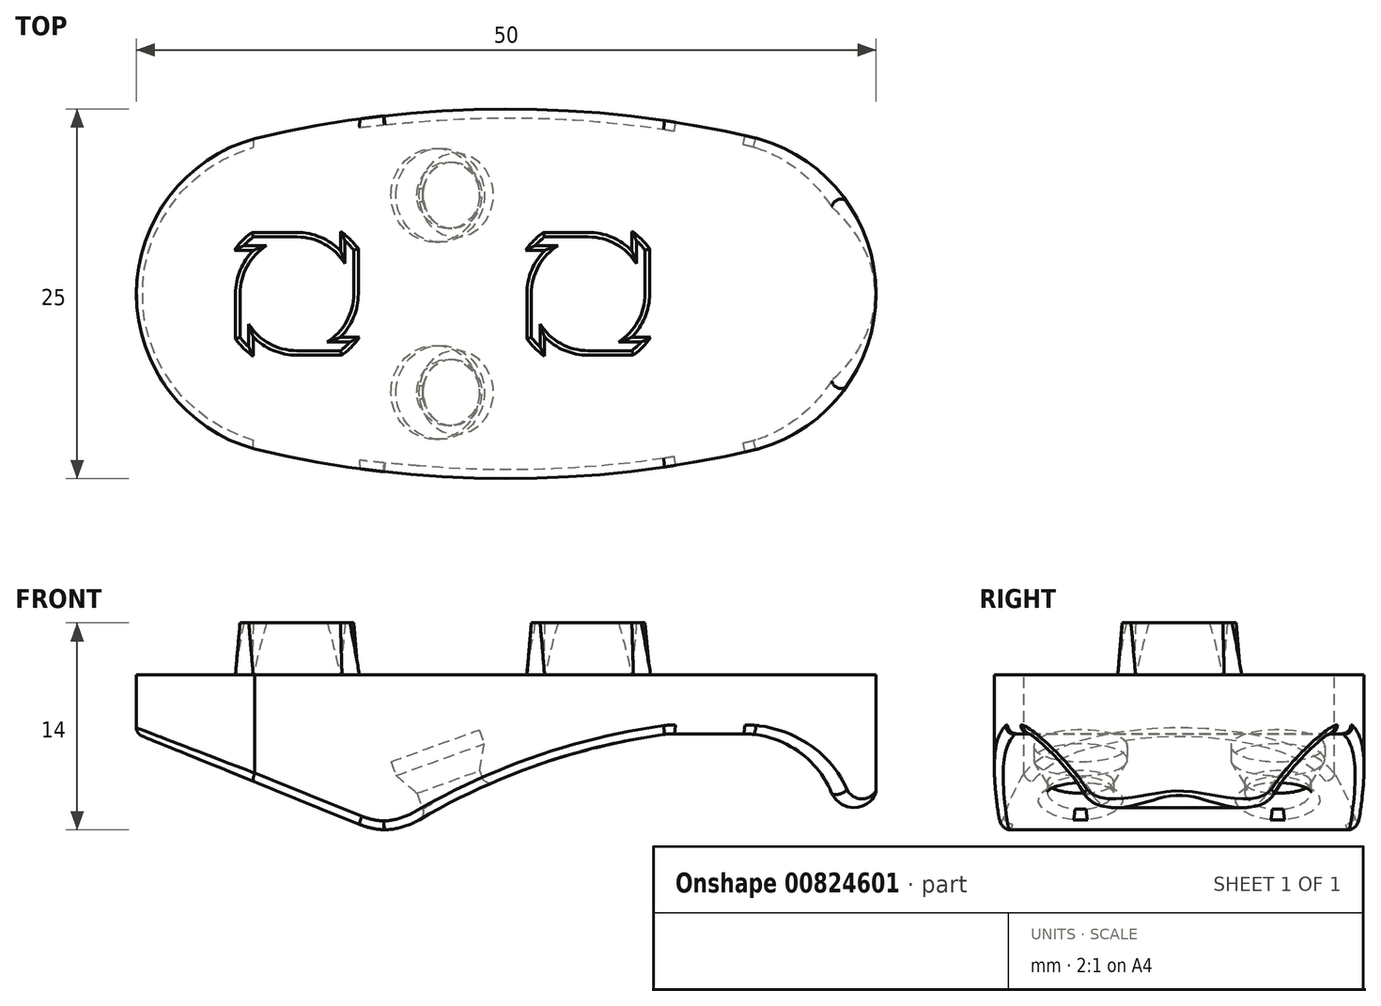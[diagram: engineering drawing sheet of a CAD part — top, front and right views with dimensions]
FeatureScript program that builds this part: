
annotation { "Feature Type Name" : "Feature", "Feature Type Description" : "" }
export const myFeature = defineFeature(function(context is Context, id is Id, definition is map)
    precondition{}
    {
        {
            var Q0;
            Q0=qCreatedBy(makeId("Front.planeOp"),FACE);
            var sketch = newSketch(context, id + "F0", { "sketchPlane" : qUnion([Q0])});
            skLineSegment(sketch, "E0", {"start": v(-12.96, 5.46) * mm, "end": v(25.04, 5.46) * mm});
            skLineSegment(sketch, "E1", {"start": v(-12.96, -7.8) * mm, "end": v(-11.16, -3.1) * mm, "construction": true});
            skLineSegment(sketch, "E2", {"start": v(-12.96, -7.8) * mm, "end": v(-12.96, 5.46) * mm});
            skLineSegment(sketch, "E3", {"start": v(0, 0) * mm, "end": v(4.11, 0) * mm});
            skArc(sketch, "E4", {"start": v(0, 0) * mm, "mid": v(-5.8, -0.8) * mm, "end": v(-11.16, -3.1) * mm});
            skArc(sketch, "E5", {"start": v(20.4, -4.8) * mm, "mid": v(12.6, -1.23) * mm, "end": v(4.11, 0) * mm});
            skLineSegment(sketch, "E6", {"start": v(20.4, -4.8) * mm, "end": v(25.04, -7.8) * mm, "construction": true});
            skLineSegment(sketch, "E7", {"start": v(25.04, -7.8) * mm, "end": v(25.04, 5.46) * mm});
            skLineSegment(sketch, "E8", {"start": v(-12.96, 3.26) * mm, "end": v(25.04, 5.46) * mm});
            skArc(sketch, "E9", {"start": v(-12.96, -3.1) * mm, "mid": v(-12.06, -3.73) * mm, "end": v(-11.16, -3.1) * mm});
            skLineSegment(sketch, "E10", {"start": v(18.4, -3.62) * mm, "end": v(25.04, -7) * mm});
            skLineSegment(sketch, "E11", {"start": v(25.04, -7) * mm, "end": v(30.04, -9.56) * mm});
            skLineSegment(sketch, "E12", {"start": v(30.04, -9.56) * mm, "end": v(30.04, 5.75) * mm});
            skLineSegment(sketch, "E13", {"start": v(25.04, 5.46) * mm, "end": v(30.04, 5.75) * mm});
            skSolve(sketch);
        }
        {
            var Q0;
            Q0=qCreatedBy(makeId("Front.planeOp"),FACE);
            var sketch = newSketch(context, id + "F1", { "sketchPlane" : qUnion([Q0])});
            skLineSegment(sketch, "E14.bottom", {"start": v(-18, 0) * mm, "end": v(18, 0) * mm});
            skLineSegment(sketch, "E14.top", {"start": v(-18, -8.5) * mm, "end": v(18, -8.5) * mm});
            skLineSegment(sketch, "E14.left", {"start": v(-18, 0) * mm, "end": v(-18, -8.5) * mm});
            skLineSegment(sketch, "E14.right", {"start": v(18, 0) * mm, "end": v(18, -8.5) * mm, "construction": true});
            skArc(sketch, "E15", {"start": v(18, -2) * mm, "mid": v(8.65, -4.28) * mm, "end": v(0, -8.5) * mm});
            skLineSegment(sketch, "E16", {"start": v(-2, -8.5) * mm, "end": v(-18, -2) * mm});
            skLineSegment(sketch, "E17", {"start": v(18, 0) * mm, "end": v(23, 0) * mm});
            skLineSegment(sketch, "E18", {"start": v(23, 0) * mm, "end": v(23, -2) * mm, "construction": true});
            skLineSegment(sketch, "E19", {"start": v(23, -2) * mm, "end": v(18, -2) * mm});
            skArc(sketch, "E20", {"start": v(29, -6) * mm, "mid": v(26.6, -3.1) * mm, "end": v(23, -2) * mm});
            skArc(sketch, "E21", {"start": v(29, -6) * mm, "mid": v(30.5, -7) * mm, "end": v(32, -6) * mm});
            skLineSegment(sketch, "E22", {"start": v(32, -6) * mm, "end": v(32, 0) * mm, "construction": true});
            skLineSegment(sketch, "E23", {"start": v(32, 0) * mm, "end": v(23, 0) * mm});
            skArc(sketch, "E24", {"start": v(32, -6) * mm, "mid": v(32.6, -3) * mm, "end": v(32, 0) * mm});
            skSolve(sketch);
        }
        {
            var Q0;
            {var subQ1=sQuery(id+"F1.wireOp",EDGE,"E14.bottom");Q0=makeQuery(id+"F1.imprint","IMPRINT",FACE,{"disambiguationData":[TD([[makeQuery(id+"F1.imprint","IMPRINT",EDGE,{"derivedFrom":subQ1}),-1.0]])]});}
            extrude(context, id + "F2", {"entities" : qUnion([Q0]), "depth" : 25 * mm, "offsetDistance" : 25 * mm});
        }
        {
            var Q0;
            Q0=makeQuery(id+"F2.opExtrude","SWEPT_FACE",FACE,{"disambiguationData":[OSD([sQuery(id+"F1.wireOp",EDGE,"E14.bottom"),sQuery(id+"F1.wireOp",EDGE,"E17"),sQuery(id+"F1.wireOp",EDGE,"E23")])]});
            var sketch = newSketch(context, id + "F3", { "sketchPlane" : qUnion([Q0])});
            skArc(sketch, "E25", {"start": v(-10, -2) * mm, "mid": v(-18, -12.5) * mm, "end": v(-10, -23) * mm});
            skArc(sketch, "E26", {"start": v(-10, -23) * mm, "mid": v(7, -25) * mm, "end": v(24, -23) * mm});
            skArc(sketch, "E27", {"start": v(24, -2) * mm, "mid": v(7, 0) * mm, "end": v(-10, -2) * mm});
            skArc(sketch, "E28", {"start": v(24, -23) * mm, "mid": v(32, -12.5) * mm, "end": v(24, -2) * mm});
            skLineSegment(sketch, "E29", {"start": v(-10, -23) * mm, "end": v(-10, -2) * mm, "construction": true});
            skLineSegment(sketch, "E30", {"start": v(-10, -23) * mm, "end": v(-10, -25) * mm, "construction": true});
            skLineSegment(sketch, "E31", {"start": v(-10, -2) * mm, "end": v(-10, 0) * mm, "construction": true});
            skLineSegment(sketch, "E32", {"start": v(-18, -12.5) * mm, "end": v(-18, -12.5) * mm});
            skPoint(sketch, "E32.startSnap0", {"position": v(-10, -12.5) * mm});
            skLineSegment(sketch, "E33.bottom", {"start": v(-18, -25) * mm, "end": v(-20.83, -25) * mm});
            skLineSegment(sketch, "E33.top", {"start": v(-18, 0) * mm, "end": v(-20.83, 0) * mm});
            skLineSegment(sketch, "E33.right", {"start": v(-20.83, -25) * mm, "end": v(-20.83, 0) * mm});
            skLineSegment(sketch, "E34.bottom", {"start": v(32, 0) * mm, "end": v(33.71, 0) * mm});
            skLineSegment(sketch, "E34.top", {"start": v(32, -25) * mm, "end": v(33.71, -25) * mm});
            skLineSegment(sketch, "E34.right", {"start": v(33.71, 0) * mm, "end": v(33.71, -25) * mm});
            skLineSegment(sketch, "E35", {"start": v(32, -12.5) * mm, "end": v(32, -12.5) * mm});
            skLineSegment(sketch, "E36", {"start": v(24, -23) * mm, "end": v(24, -25) * mm, "construction": true});
            skLineSegment(sketch, "E37", {"start": v(24, -2) * mm, "end": v(24, 0) * mm, "construction": true});
            skSolve(sketch);
        }
        {
            var Q0;
            {var subQ1=sQuery(id+"F3.wireOp",EDGE,"E26");Q0=makeQuery(id+"F3.imprint","IMPRINT",FACE,{"disambiguationData":[TD([[makeQuery(id+"F3.imprint","IMPRINT",EDGE,{"derivedFrom":subQ1}),-1.0]])]});}
            var Q1;
            {var subQ2=sQuery(id+"F3.wireOp",EDGE,"E27");Q1=makeQuery(id+"F3.imprint","IMPRINT",FACE,{"disambiguationData":[TD([[makeQuery(id+"F3.imprint","IMPRINT",EDGE,{"derivedFrom":subQ2}),-1.0]])]});}
            var Q2;
            {var subQ1=sQuery(id+"F3.wireOp",EDGE,"E34.bottom");Q2=makeQuery(id+"F3.imprint","IMPRINT",FACE,{"disambiguationData":[TD([[makeQuery(id+"F3.imprint","IMPRINT",EDGE,{"derivedFrom":subQ1}),-1.0]])]});}
            var Q3;
            {var subQ1=sQuery(id+"F3.wireOp",EDGE,"E33.bottom");Q3=makeQuery(id+"F3.imprint","IMPRINT",FACE,{"disambiguationData":[TD([[makeQuery(id+"F3.imprint","IMPRINT",EDGE,{"derivedFrom":subQ1}),-1.0]])]});}
            extrude(context, id + "F4", {"entities" : qUnion([Q0, Q1, Q2, Q3]), "operationType" : NewBodyOperationType.REMOVE, "oppositeDirection" : true, "depth" : 25 * mm, "offsetDistance" : 25 * mm});
        }
        {
            var Q0;
            {var subQ0=sQuery(id+"F3.wireOp",EDGE,"E26");Q0=makeQuery(id+"F4.boolean.opBoolean","INTERSECT",VERTEX,{"derivedFrom":[makeQuery(id+"F2.opExtrude","SWEPT_FACE",FACE,{"disambiguationData":[OSD([sQuery(id+"F1.wireOp",EDGE,"E14.top")])]}),makeQuery(id+"F2.opExtrude","SWEPT_FACE",FACE,{"disambiguationData":[OSD([sQuery(id+"F1.wireOp",EDGE,"E15")])]}),makeQuery(id+"F4.opExtrude","SWEPT_FACE",FACE,{"disambiguationData":[OSD([subQ0]),TDD([makeQuery(id+"F3.imprint","IMPRINT",EDGE,{"disambiguationData":[TD([[makeQuery(id+"F3.imprint","INTERSECT",VERTEX,{"derivedFrom":[sQuery(id+"F3.wireOp",EDGE,"E25"),subQ0]}),-1.0]])],"derivedFrom":subQ0})])]}),makeQuery(id+"F4.opExtrude","SWEPT_FACE",FACE,{"disambiguationData":[OSD([subQ0]),TDD([makeQuery(id+"F3.imprint","IMPRINT",EDGE,{"disambiguationData":[TD([[makeQuery(id+"F3.imprint","INTERSECT",VERTEX,{"derivedFrom":[subQ0,sQuery(id+"F3.wireOp",EDGE,"E28")]}),1.0]])],"derivedFrom":subQ0})])]})]});}
            var Q1;
            {var subQ0=sQuery(id+"F3.wireOp",EDGE,"E26");Q1=makeQuery(id+"F4.boolean.opBoolean","INTERSECT",VERTEX,{"derivedFrom":[makeQuery(id+"F2.opExtrude","SWEPT_FACE",FACE,{"disambiguationData":[OSD([sQuery(id+"F1.wireOp",EDGE,"E15")])]}),makeQuery(id+"F2.opExtrude","SWEPT_FACE",FACE,{"disambiguationData":[OSD([sQuery(id+"F1.wireOp",EDGE,"E19")])]}),makeQuery(id+"F4.opExtrude","SWEPT_FACE",FACE,{"disambiguationData":[OSD([subQ0]),TDD([makeQuery(id+"F3.imprint","IMPRINT",EDGE,{"disambiguationData":[TD([[makeQuery(id+"F3.imprint","INTERSECT",VERTEX,{"derivedFrom":[sQuery(id+"F3.wireOp",EDGE,"E25"),subQ0]}),-1.0]])],"derivedFrom":subQ0})])]}),makeQuery(id+"F4.opExtrude","SWEPT_FACE",FACE,{"disambiguationData":[OSD([subQ0]),TDD([makeQuery(id+"F3.imprint","IMPRINT",EDGE,{"disambiguationData":[TD([[makeQuery(id+"F3.imprint","INTERSECT",VERTEX,{"derivedFrom":[subQ0,sQuery(id+"F3.wireOp",EDGE,"E28")]}),1.0]])],"derivedFrom":subQ0})])]})]});}
            var Q2;
            {var subQ0=sQuery(id+"F3.wireOp",EDGE,"E27");Q2=makeQuery(id+"F4.boolean.opBoolean","INTERSECT",VERTEX,{"derivedFrom":[makeQuery(id+"F2.opExtrude","SWEPT_FACE",FACE,{"disambiguationData":[OSD([sQuery(id+"F1.wireOp",EDGE,"E14.top")])]}),makeQuery(id+"F2.opExtrude","SWEPT_FACE",FACE,{"disambiguationData":[OSD([sQuery(id+"F1.wireOp",EDGE,"E15")])]}),makeQuery(id+"F4.opExtrude","SWEPT_FACE",FACE,{"disambiguationData":[OSD([subQ0]),TDD([makeQuery(id+"F3.imprint","IMPRINT",EDGE,{"disambiguationData":[TD([[makeQuery(id+"F3.imprint","INTERSECT",VERTEX,{"derivedFrom":[subQ0,sQuery(id+"F3.wireOp",EDGE,"E28")]}),-1.0]])],"derivedFrom":subQ0})])]}),makeQuery(id+"F4.opExtrude","SWEPT_FACE",FACE,{"disambiguationData":[OSD([subQ0]),TDD([makeQuery(id+"F3.imprint","IMPRINT",EDGE,{"disambiguationData":[TD([[makeQuery(id+"F3.imprint","INTERSECT",VERTEX,{"derivedFrom":[sQuery(id+"F3.wireOp",EDGE,"E25"),subQ0]}),1.0]])],"derivedFrom":subQ0})])]})]});}
            cPlane(context, id + "F5", {"entities" : qUnion([Q0, Q1, Q2]), "cplaneType" : CPlaneType.THREE_POINT, "offset" : 25 * mm, "width" : 150 * mm, "height" : 150 * mm});
        }
        {
            var Q0;
            Q0=qCreatedBy(id+"F5.planeOp",FACE);
            var sketch = newSketch(context, id + "F6", { "sketchPlane" : qUnion([Q0])});
            skCircle(sketch, "E38", {"center": v(1.11, 19.17) * mm, "radius": 2.25 * mm});
            skCircle(sketch, "E39", {"center": v(1.11, 5.83) * mm, "radius": 2.25 * mm});
            skLineSegment(sketch, "E40", {"start": v(1.11, 24.92) * mm, "end": v(1.11, 21.42) * mm, "construction": true});
            skLineSegment(sketch, "E41", {"start": v(1.11, 0.08) * mm, "end": v(1.11, 3.58) * mm, "construction": true});
            skSolve(sketch);
        }
        {
            var Q0;
            {var subQ0=sQuery(id+"F6.wireOp",EDGE,"E39");var subQ1=makeQuery(id+"FXYdpxftjrvMDqK_0.opExtrude","SWEPT_EDGE",EDGE,{"disambiguationData":[OSD([sQuery(id+"F0.wireOp",EDGE,"E5"),sQuery(id+"F0.wireOp",EDGE,"E10")])]});var subQ2=makeQuery(id+"F6.imprint","INTERSECT",VERTEX,{"disambiguationData":[OD(0.0)],"derivedFrom":[subQ1,subQ0]});Q0=makeQuery(id+"F6.imprint","IMPRINT",FACE,{"disambiguationData":[TD([[makeQuery(id+"F6.imprint","IMPRINT",EDGE,{"disambiguationData":[TD([[subQ2,-1.0]])],"derivedFrom":subQ0}),1.0]])]});}
            var Q1;
            {var subQ0=sQuery(id+"F6.wireOp",EDGE,"E39");var subQ1=makeQuery(id+"FXYdpxftjrvMDqK_0.opExtrude","SWEPT_EDGE",EDGE,{"disambiguationData":[OSD([sQuery(id+"F0.wireOp",EDGE,"E5"),sQuery(id+"F0.wireOp",EDGE,"E10")])]});var subQ2=makeQuery(id+"F6.imprint","INTERSECT",VERTEX,{"disambiguationData":[OD(0.0)],"derivedFrom":[subQ1,subQ0]});Q1=makeQuery(id+"F6.imprint","IMPRINT",FACE,{"disambiguationData":[TD([[makeQuery(id+"F6.imprint","IMPRINT",EDGE,{"disambiguationData":[TD([[subQ2,1.0]])],"derivedFrom":subQ0}),1.0]])]});}
            var Q2;
            {var subQ0=sQuery(id+"F6.wireOp",EDGE,"E38");var subQ1=makeQuery(id+"FXYdpxftjrvMDqK_0.opExtrude","SWEPT_EDGE",EDGE,{"disambiguationData":[OSD([sQuery(id+"F0.wireOp",EDGE,"E5"),sQuery(id+"F0.wireOp",EDGE,"E10")])]});var subQ2=makeQuery(id+"F6.imprint","INTERSECT",VERTEX,{"disambiguationData":[OD(0.0)],"derivedFrom":[subQ1,subQ0]});Q2=makeQuery(id+"F6.imprint","IMPRINT",FACE,{"disambiguationData":[TD([[makeQuery(id+"F6.imprint","IMPRINT",EDGE,{"disambiguationData":[TD([[subQ2,-1.0]])],"derivedFrom":subQ0}),1.0]])]});}
            var Q3;
            {var subQ0=sQuery(id+"F6.wireOp",EDGE,"E38");var subQ1=makeQuery(id+"FXYdpxftjrvMDqK_0.opExtrude","SWEPT_EDGE",EDGE,{"disambiguationData":[OSD([sQuery(id+"F0.wireOp",EDGE,"E5"),sQuery(id+"F0.wireOp",EDGE,"E10")])]});var subQ2=makeQuery(id+"F6.imprint","INTERSECT",VERTEX,{"disambiguationData":[OD(0.0)],"derivedFrom":[subQ1,subQ0]});Q3=makeQuery(id+"F6.imprint","IMPRINT",FACE,{"disambiguationData":[TD([[makeQuery(id+"F6.imprint","IMPRINT",EDGE,{"disambiguationData":[TD([[subQ2,1.0]])],"derivedFrom":subQ0}),1.0]])]});}
            extrude(context, id + "F7", {"entities" : qUnion([Q0, Q1, Q2, Q3]), "operationType" : NewBodyOperationType.REMOVE, "oppositeDirection" : true, "depth" : 2 * mm, "offsetDistance" : 25 * mm, "hasSecondDirection" : true, "secondDirectionOppositeDirection" : false, "secondDirectionDepth" : 25 * mm});
        }
        {
            var Q0;
            Q0=makeQuery(id+"F7.boolean.opBoolean","COPY",FACE,{"derivedFrom":makeQuery(id+"F7.opExtrude","CAP_FACE",FACE,{"disambiguationData":[OSD([sQuery(id+"F6.wireOp",EDGE,"E39")])],"isStart":false})});
            var Q1;
            Q1=makeQuery(id+"F7.boolean.opBoolean","COPY",FACE,{"derivedFrom":makeQuery(id+"F7.opExtrude","CAP_FACE",FACE,{"disambiguationData":[OSD([sQuery(id+"F6.wireOp",EDGE,"E38")])],"isStart":false})});
            extrude(context, id + "F8", {"entities" : qUnion([Q0, Q1]), "operationType" : NewBodyOperationType.REMOVE, "oppositeDirection" : true, "depth" : 1.6 * mm, "offsetDistance" : 25 * mm, "hasDraft" : true, "draftAngle" : 30 * degree});
        }
        {
            var Q0;
            Q0=makeQuery(id+"F8.boolean.opBoolean","COPY",FACE,{"derivedFrom":makeQuery(id+"F8.opExtrude","CAP_FACE",FACE,{"disambiguationData":[OSD([sQuery(id+"F6.wireOp",EDGE,"E38")])],"isStart":false})});
            var Q1;
            Q1=makeQuery(id+"F8.boolean.opBoolean","COPY",FACE,{"derivedFrom":makeQuery(id+"F8.opExtrude","CAP_FACE",FACE,{"disambiguationData":[OSD([sQuery(id+"F6.wireOp",EDGE,"E39")])],"isStart":false})});
            extrude(context, id + "F9", {"entities" : qUnion([Q0, Q1]), "operationType" : NewBodyOperationType.REMOVE, "oppositeDirection" : true, "depth" : 1 * mm, "offsetDistance" : 25 * mm});
        }
        {
            var Q0;
            Q0=makeQuery(id+"F2.opExtrude","SWEPT_FACE",FACE,{"disambiguationData":[OSD([sQuery(id+"F1.wireOp",EDGE,"E14.bottom"),sQuery(id+"F1.wireOp",EDGE,"E17"),sQuery(id+"F1.wireOp",EDGE,"E23")])]});
            extrude(context, id + "F10", {"entities" : qUnion([Q0]), "operationType" : NewBodyOperationType.ADD, "depth" : 2 * mm, "offsetDistance" : 25 * mm});
        }
        {
            var Q0;
            Q0=makeQuery(id+"F10.opExtrude","CAP_FACE",FACE,{"disambiguationData":[OSD([sQuery(id+"F1.wireOp",EDGE,"E14.bottom"),sQuery(id+"F1.wireOp",EDGE,"E17"),sQuery(id+"F1.wireOp",EDGE,"E23")])],"isStart":false});
            var sketch = newSketch(context, id + "F11", { "sketchPlane" : qUnion([Q0])});
            skCircle(sketch, "E42", {"center": v(-7.15, -12.5) * mm, "radius": 5.15 * mm});
            skCircle(sketch, "E43", {"center": v(12.55, -12.5) * mm, "radius": 5.15 * mm});
            skPoint(sketch, "E44", {"position": v(-18, -12.5) * mm});
            skLineSegment(sketch, "E45", {"start": v(12.55, -12.5) * mm, "end": v(-7.15, -12.5) * mm, "construction": true});
            skLineSegment(sketch, "E46", {"start": v(-12.3, -12.5) * mm, "end": v(-18, -12.5) * mm, "construction": true});
            skLineSegment(sketch, "E47", {"start": v(32, -12.5) * mm, "end": v(17.7, -12.5) * mm, "construction": true});
            skArc(sketch, "E48", {"start": v(9.63, -9.55) * mm, "mid": v(8.72, -10.9) * mm, "end": v(8.4, -12.5) * mm});
            skArc(sketch, "E49", {"start": v(-4.23, -15.45) * mm, "mid": v(-3.32, -14.1) * mm, "end": v(-3, -12.5) * mm});
            skLineSegment(sketch, "E50", {"start": v(12.55, -8.35) * mm, "end": v(9.5, -8.35) * mm});
            skLineSegment(sketch, "E51", {"start": v(9.63, -9.55) * mm, "end": v(8.33, -9.55) * mm});
            skLineSegment(sketch, "E52.1.0", {"start": v(9.6, -15.42) * mm, "end": v(9.6, -16.72) * mm});
            skLineSegment(sketch, "E52.1.1", {"start": v(8.4, -12.5) * mm, "end": v(8.4, -15.55) * mm});
            skLineSegment(sketch, "E52.2.0", {"start": v(15.47, -15.45) * mm, "end": v(16.77, -15.45) * mm});
            skLineSegment(sketch, "E52.2.1", {"start": v(12.55, -16.65) * mm, "end": v(15.6, -16.65) * mm});
            skLineSegment(sketch, "E52.3.0", {"start": v(15.5, -9.58) * mm, "end": v(15.5, -8.28) * mm});
            skLineSegment(sketch, "E52.3.1", {"start": v(16.7, -12.5) * mm, "end": v(16.7, -9.45) * mm});
            skArc(sketch, "E53.trimOffspring", {"start": v(9.6, -15.42) * mm, "mid": v(10.95, -16.33) * mm, "end": v(12.55, -16.65) * mm});
            skArc(sketch, "E54.trimOffspring", {"start": v(15.47, -15.45) * mm, "mid": v(16.38, -14.1) * mm, "end": v(16.7, -12.5) * mm});
            skArc(sketch, "E55.trimOffspring", {"start": v(15.5, -9.58) * mm, "mid": v(14.15, -8.67) * mm, "end": v(12.55, -8.35) * mm});
            skLineSegment(sketch, "E56", {"start": v(-7.15, -8.35) * mm, "end": v(-10.2, -8.35) * mm});
            skLineSegment(sketch, "E57", {"start": v(-10.07, -9.55) * mm, "end": v(-11.37, -9.55) * mm});
            skLineSegment(sketch, "E58.1.0", {"start": v(-11.3, -12.5) * mm, "end": v(-11.3, -15.55) * mm});
            skLineSegment(sketch, "E58.1.1", {"start": v(-10.1, -15.42) * mm, "end": v(-10.1, -16.72) * mm});
            skLineSegment(sketch, "E58.2.0", {"start": v(-7.15, -16.65) * mm, "end": v(-4.1, -16.65) * mm});
            skLineSegment(sketch, "E58.2.1", {"start": v(-4.23, -15.45) * mm, "end": v(-2.93, -15.45) * mm});
            skLineSegment(sketch, "E58.3.0", {"start": v(-3, -12.5) * mm, "end": v(-3, -9.45) * mm});
            skLineSegment(sketch, "E58.3.1", {"start": v(-4.2, -9.58) * mm, "end": v(-4.2, -8.28) * mm});
            skArc(sketch, "E59.trimOffspring", {"start": v(-4.2, -9.58) * mm, "mid": v(-5.55, -8.67) * mm, "end": v(-7.15, -8.35) * mm});
            skArc(sketch, "E60.trimOffspring", {"start": v(-10.07, -9.55) * mm, "mid": v(-10.98, -10.9) * mm, "end": v(-11.3, -12.5) * mm});
            skArc(sketch, "E61.trimOffspring", {"start": v(-10.1, -15.42) * mm, "mid": v(-8.75, -16.33) * mm, "end": v(-7.15, -16.65) * mm});
            skSolve(sketch);
        }
        {
            var Q0;
            Q0=makeQuery(id+"F11.imprint","IMPRINT",FACE,{"disambiguationData":[TD([[makeQuery(id+"F11.imprint","IMPRINT",EDGE,{"derivedFrom":sQuery(id+"F11.wireOp",EDGE,"E49")}),1.0]])]});
            var Q1;
            Q1=makeQuery(id+"F11.imprint","IMPRINT",FACE,{"disambiguationData":[TD([[makeQuery(id+"F11.imprint","IMPRINT",EDGE,{"derivedFrom":sQuery(id+"F11.wireOp",EDGE,"E48")}),1.0]])]});
            extrude(context, id + "F12", {"entities" : qUnion([Q0, Q1]), "operationType" : NewBodyOperationType.ADD, "depth" : 3.5 * mm, "offsetDistance" : 25 * mm, "hasDraft" : true, "draftAngle" : 5 * degree, "draftPullDirection" : true});
        }
        {
            var Q0;
            Q0=makeQuery(id+"F2.opExtrude","SWEPT_EDGE",EDGE,{"disambiguationData":[OSD([sQuery(id+"F1.wireOp",EDGE,"E14.top"),sQuery(id+"F1.wireOp",EDGE,"E15")])]});
            var Q1;
            Q1=makeQuery(id+"F2.opExtrude","SWEPT_EDGE",EDGE,{"disambiguationData":[OSD([sQuery(id+"F1.wireOp",EDGE,"E14.top"),sQuery(id+"F1.wireOp",EDGE,"E16")])]});
            var Q2;
            Q2=makeQuery(id+"F2.opExtrude","SWEPT_EDGE",EDGE,{"disambiguationData":[OSD([sQuery(id+"F1.wireOp",EDGE,"E15"),sQuery(id+"F1.wireOp",EDGE,"E19")])]});
            var Q3;
            Q3=makeQuery(id+"F2.opExtrude","SWEPT_EDGE",EDGE,{"disambiguationData":[OSD([sQuery(id+"F1.wireOp",EDGE,"E19"),sQuery(id+"F1.wireOp",EDGE,"E20")])]});
            var Q4;
            {var subQ0=sQuery(id+"F3.wireOp",EDGE,"E28");var subQ1=sQuery(id+"F3.wireOp",EDGE,"E27");Q4=makeQuery(id+"F10.boolean.opBoolean","MERGE",EDGE,{"derivedFrom":[makeQuery(id+"F4.boolean.opBoolean","COPY",EDGE,{"derivedFrom":makeQuery(id+"F4.opExtrude","SWEPT_EDGE",EDGE,{"disambiguationData":[OSD([subQ1,subQ0])]})}),makeQuery(id+"F10.opExtrude","SWEPT_EDGE",EDGE,{"disambiguationData":[OSD([subQ1,subQ0])]})]});}
            var Q5;
            {var subQ0=sQuery(id+"F3.wireOp",EDGE,"E28");var subQ1=sQuery(id+"F3.wireOp",EDGE,"E26");Q5=makeQuery(id+"F10.boolean.opBoolean","MERGE",EDGE,{"derivedFrom":[makeQuery(id+"F4.boolean.opBoolean","COPY",EDGE,{"derivedFrom":makeQuery(id+"F4.opExtrude","SWEPT_EDGE",EDGE,{"disambiguationData":[OSD([subQ1,subQ0])]})}),makeQuery(id+"F10.opExtrude","SWEPT_EDGE",EDGE,{"disambiguationData":[OSD([subQ1,subQ0])]})]});}
            fillet(context, id + "F13", {"entities" : qUnion([Q0, Q1, Q2, Q3, Q4, Q5]), "radius" : 5 * mm, "tangentPropagation" : true, "allowEdgeOverflow" : false});
        }
        {
            var Q0;
            Q0=makeQuery(id+"F2.opExtrude","SWEPT_FACE",FACE,{"disambiguationData":[OSD([sQuery(id+"F1.wireOp",EDGE,"E15")])]});
            var Q1;
            Q1=makeQuery(id+"F13.opFillet","BLEND_FACE",FACE,{"disambiguationData":[OSD([sQuery(id+"F1.wireOp",EDGE,"E14.top"),sQuery(id+"F1.wireOp",EDGE,"E15")])]});
            var Q2;
            Q2=makeQuery(id+"F13.opFillet","BLEND_FACE",FACE,{"disambiguationData":[OSD([sQuery(id+"F1.wireOp",EDGE,"E14.top"),sQuery(id+"F1.wireOp",EDGE,"E16")])]});
            var Q3;
            Q3=makeQuery(id+"F2.opExtrude","SWEPT_FACE",FACE,{"disambiguationData":[OSD([sQuery(id+"F1.wireOp",EDGE,"E16")])]});
            var Q4;
            Q4=makeQuery(id+"F2.opExtrude","SWEPT_FACE",FACE,{"disambiguationData":[OSD([sQuery(id+"F1.wireOp",EDGE,"E20")])]});
            var Q5;
            Q5=makeQuery(id+"F2.opExtrude","SWEPT_FACE",FACE,{"disambiguationData":[OSD([sQuery(id+"F1.wireOp",EDGE,"E21")])]});
            var Q6;
            Q6=makeQuery(id+"F2.opExtrude","SWEPT_FACE",FACE,{"disambiguationData":[OSD([sQuery(id+"F1.wireOp",EDGE,"E19")])]});
            fillet(context, id + "F14", {"entities" : qUnion([Q0, Q1, Q2, Q3, Q4, Q5, Q6]), "radius" : 0.6 * mm, "tangentPropagation" : true, "allowEdgeOverflow" : false});
        }
    });
